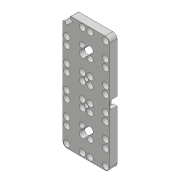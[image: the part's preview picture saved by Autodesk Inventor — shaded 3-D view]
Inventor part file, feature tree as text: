
AUTODESK INVENTOR PART (.ipt)
format: ipt  version: 2018 (Build 220112000, 112)  size: 1,013,248 bytes
history: native  units: mm
features: projected_geometry x15, extrude x13, sketch x12, fillet x7, pattern_linear x6
ambient origin geometry x8: Origin, YZ Plane, XZ Plane, XY Plane, X Axis, Y Axis, Z Axis, Center Point
bodies: Solid1 (feature_tree)
feature tree (53):
  extrude  "Extrusion1"  Depth=44.0mm
  extrude  "Extrusion2"  Depth=22.0mm
  extrude  "Extrusion3"  Depth=22.0mm
  pattern_linear  "Rectangular Pattern1"  Count1=5 Spacing1=22.0mm
  extrude  "Extrusion4"  Depth=10.0mm
  pattern_linear  "Rectangular Pattern2"  Spacing1=5.0mm  [1 undecoded]
  extrude  "Extrusion5"  Depth=5.0mm
  pattern_linear  "Rectangular Pattern3"  Spacing1=2.0mm  [1 undecoded]
  fillet  "Fillet1"  Radius=50.0mm
  extrude  "Extrusion6"  Depth=2.0mm TaperAngle=0.0deg
  extrude  "Extrusion9"  Depth=22.0mm
  pattern_linear  "Rectangular Pattern4"  Spacing1=1.0mm  [1 undecoded]
  extrude  "Extrusion7"  Depth=1.0mm
  pattern_linear  "Rectangular Pattern5"  Spacing1=6.7mm  [1 undecoded]
  pattern_linear  "Rectangular Pattern6"  Count1=2 Spacing1=66.0mm
  fillet  "Fillet2"  Radius=4.0mm
  fillet  "Fillet3"  Radius=2.0mm
  fillet  "Fillet4"  Radius=22.0mm
  extrude  "Extrusion8"  Depth=4.0mm
  fillet  "Fillet5"  Radius=0.5mm
  extrude  "Extrusion10"  Depth=1.0mm
  extrude  "Extrusion11"  Depth=2.5mm
  fillet  "Fillet6"  Radius=3.0mm
  extrude  "Extrusion12"  Depth=0.5mm
  extrude  "Extrusion13"  Depth=2.0mm
  fillet  "Fillet7"  Radius=2.0mm
  sketch  "Sketch1"  dims[d0=110.0mm d1=44.0mm]
  sketch  "Sketch2"  dims[d2=7.3mm d3=0.0mm d4=22.0mm]
  projected_geometry  "Projected Loop1"
  sketch  "Sketch3"  dims[d5=22.0mm d6=14.75mm]
  projected_geometry  "Projected Loop2"
  projected_geometry  "Projected Loop3"
  projected_geometry  "Projected Loop4"
  projected_geometry  "Projected Loop5"
  sketch  "Sketch4"  dims[d7=7.5mm]
  projected_geometry  "Projected Loop6"
  sketch  "Sketch5"  dims[d8=7.0mm d9=0.0mm]
  projected_geometry  "Projected Loop7"
  projected_geometry  "Projected Loop8"
  sketch  "Sketch7"  dims[d10=6.7mm d11=0.0mm]
  projected_geometry  "Projected Loop9"
  sketch  "Sketch8"  dims[d12=6.0mm]
  projected_geometry  "Projected Loop10"
  sketch  "Sketch9"  dims[d13=6.0mm]
  sketch  "Sketch10"  dims[d14=6.0mm]
  sketch  "Sketch11"  dims[d15=6.0mm d16=50.0mm d18=22.0mm]
  projected_geometry  "Projected Loop11"
  projected_geometry  "Projected Loop12"
  projected_geometry  "Projected Loop13"
  sketch  "Sketch12"  dims[d19=20.0mm d21=22.0mm d22=10.0mm]
  projected_geometry  "Projected Loop14"
  sketch  "Sketch13"  dims[d23=5.0mm d24=5.0mm d25=5.0mm d26=2.0mm d27=0.0mm d28=50.0mm d30=22.0mm d31=2.0mm d32=0.0mm d33=20.0mm d35=22.0mm d36=1.0mm d37=8.5mm d38=6.7mm d39=0.0mm d40=20.0mm d42=66.0mm d43=4.0mm d44=2.0mm d45=0.0mm d46=20.0mm d48=22.0mm d49=4.0mm d50=0.5mm d51=1.0mm d52=2.5mm d53=3.0mm d54=0.0mm d55=0.5mm d56=2.0mm d57=2.0mm d58=2.0mm d59=2.0mm d60=2.0mm d61=2.0mm d62=2.0mm d63=2.0mm d64=10.0mm d65=0.0mm d66=40.0mm d68=22.0mm d69=8.0mm d70=10.0mm d71=0.0mm d72=10.0mm d73=0.0mm d74=2.0mm d75=45.0deg d76=18.0mm d77=7.5mm d78=10.0mm d79=0.0mm d80=4.0mm d81=12.0mm d82=0.0mm d83=0.0mm d84=1.0mm]
  projected_geometry  "Projected Loop15"
note: 4 required parameter values undecoded (feature->parameter linkage not recoverable at this tier; creation-order binding heuristic only, values carry confidence <= 0.55)
